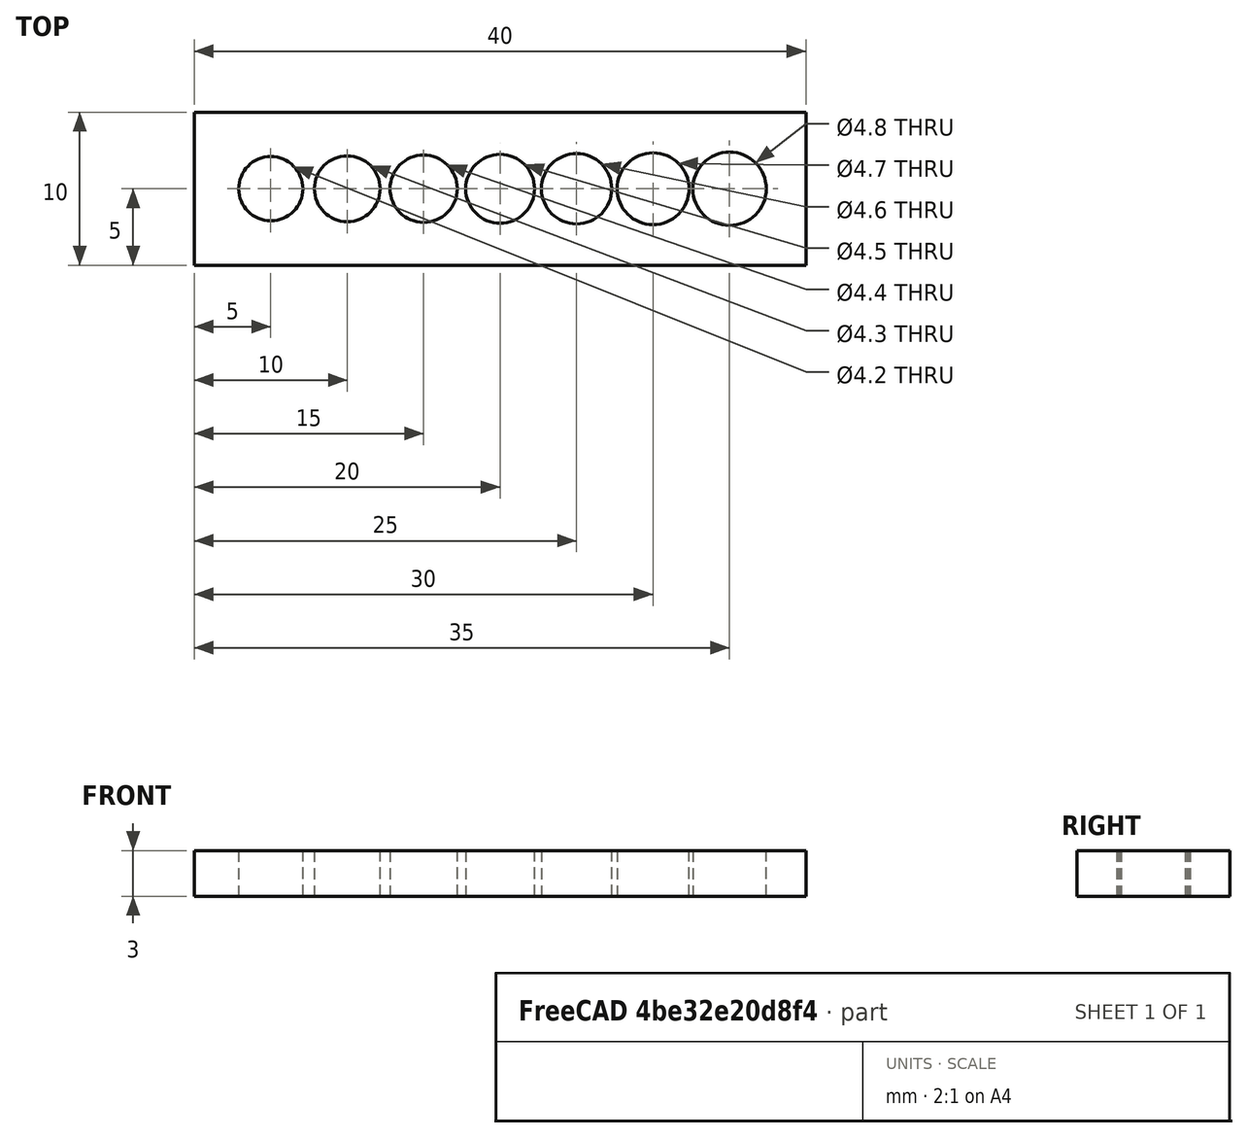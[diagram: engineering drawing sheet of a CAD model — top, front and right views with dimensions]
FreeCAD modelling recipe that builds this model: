
FCSTD DOCUMENT  (FreeCAD 0.18R16146 (Git))
Label: shaftTrial
License: All rights reserved
LicenseURL: http://en.wikipedia.org/wiki/All_rights_reserved
objects: Sketcher::SketchObject×1, PartDesign::Pad×1, PartDesign::Body×1
note: 4 computed .brp shape members not serialized (recipe doc carries the construction recipe); baked Part::Feature solids carry a one-line shape summary decoded from their .brp

FEATURE [Sketcher::SketchObject] Sketch
  MapMode = 5
  Support = -> [XY_Plane]
  sketch-geometry (12):
    g0: LineSegment StartX=-2e-16 StartY=10 StartZ=0 EndX=40 EndY=10 EndZ=0
    g1: LineSegment StartX=40 StartY=10 StartZ=0 EndX=40 EndY=0 EndZ=0
    g2: LineSegment StartX=40 StartY=0 StartZ=0 EndX=0 EndY=0 EndZ=0
    g3: LineSegment StartX=-2e-16 StartY=0 StartZ=0 EndX=-2e-16 EndY=10 EndZ=0
    g4: Circle CenterX=5 CenterY=5 CenterZ=0 NormalX=0 NormalY=0 NormalZ=1 AngleXU=0 Radius=2.1
    g5: Circle CenterX=15 CenterY=5 CenterZ=0 NormalX=0 NormalY=0 NormalZ=1 AngleXU=0 Radius=2.2
    g6: Circle CenterX=10 CenterY=5 CenterZ=0 NormalX=0 NormalY=0 NormalZ=1 AngleXU=0 Radius=2.15
    g7: Circle CenterX=20 CenterY=5 CenterZ=0 NormalX=0 NormalY=0 NormalZ=1 AngleXU=0 Radius=2.25
    g8: Circle CenterX=25 CenterY=5 CenterZ=0 NormalX=0 NormalY=0 NormalZ=1 AngleXU=0 Radius=2.3
    g9: Circle CenterX=30 CenterY=5 CenterZ=0 NormalX=0 NormalY=0 NormalZ=1 AngleXU=0 Radius=2.35
    g10: Circle CenterX=35 CenterY=5 CenterZ=0 NormalX=0 NormalY=0 NormalZ=1 AngleXU=0 Radius=2.4
    g11: LineSegment [constr] StartX=-2e-16 StartY=5 StartZ=0 EndX=40 EndY=5 EndZ=0
  constraints (36):
    c: Coincident(g0,g1)
    c: Coincident(g1,g2)
    c: Coincident(g2,g3)
    c: Coincident(g3,g0)
    c: Horizontal(g0)
    c: Horizontal(g2)
    c: Vertical(g1)
    c: Vertical(g3)
    c: Coincident(g2,g-1)
    c: Distance(g0,g0) = 40
    c: Distance(g0,g1) = 10
    c: Radius(g4) = 2.1
    c: Radius(g5) = 2.2
    c: Radius(g6) = 2.15
    c: Radius(g7) = 2.25
    c: Radius(g8) = 2.3
    c: Radius(g9) = 2.35
    c: Radius(g10) = 2.4
    c: PointOnObject(g11,g3)
    c: PointOnObject(g11,g1)
    c: Horizontal(g11)
    c: DistanceY(g2,g11) = 5
    c: PointOnObject(g4,g11)
    c: PointOnObject(g6,g11)
    c: PointOnObject(g5,g11)
    c: PointOnObject(g7,g11)
    c: PointOnObject(g8,g11)
    c: PointOnObject(g9,g11)
    c: PointOnObject(g10,g11)
    c: Distance(g4,g11) = 5
    c: Distance(g6,g4) = 5
    c: Distance(g6,g5) = 5
    c: Distance(g7,g5) = 5
    c: Distance(g8,g7) = 5
    c: Distance(g9,g8) = 5
    c: Distance(g10,g9) = 5
FEATURE [PartDesign::Pad] Pad
  Length = 3
  Length2 = 100
  Profile = -> Sketch
  Type = 0
FEATURE [PartDesign::Body] Body
  Group = -> [Sketch,Pad]
  Origin = -> Origin
  Tip = -> Pad
